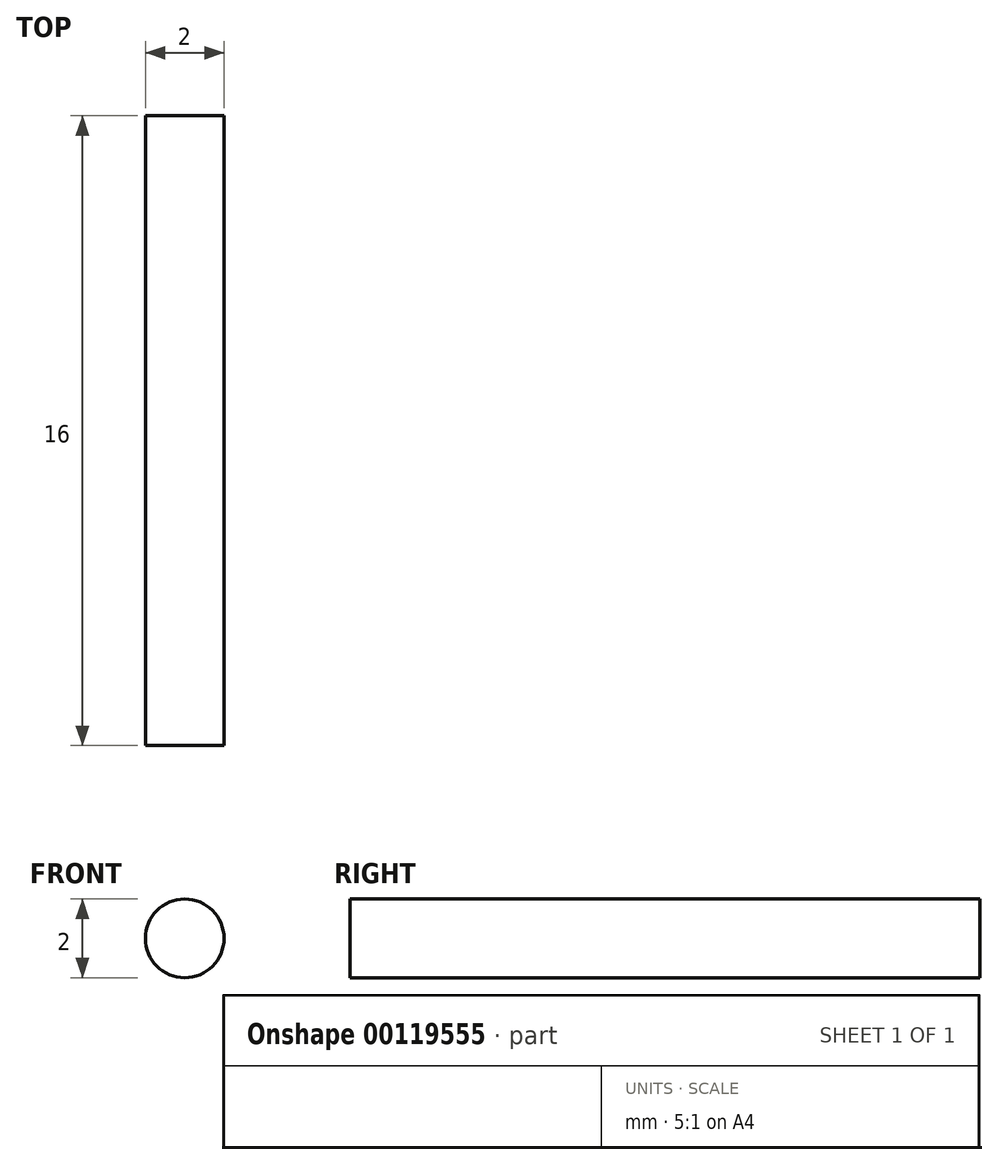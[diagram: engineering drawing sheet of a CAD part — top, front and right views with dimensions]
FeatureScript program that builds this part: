
annotation { "Feature Type Name" : "Feature", "Feature Type Description" : "" }
export const myFeature = defineFeature(function(context is Context, id is Id, definition is map)
    precondition{}
    {
        {
            var Q0;
            Q0=qCreatedBy(makeId("Front.planeOp"),FACE);
            var sketch = newSketch(context, id + "F0", { "sketchPlane" : qUnion([Q0])});
            skCircle(sketch, "E0", {"center": v(0, 0) * mm, "radius": 1 * mm});
            skSolve(sketch);
        }
        {
            var Q0;
            Q0=makeQuery(id+"F0.imprint","IMPRINT",FACE,{"disambiguationData":[TD([[makeQuery(id+"F0.imprint","IMPRINT",EDGE,{"derivedFrom":sQuery(id+"F0.wireOp",EDGE,"E0")}),1.0]])]});
            extrude(context, id + "F1", {"entities" : qUnion([Q0]), "depth" : 16 * mm});
        }
    });
